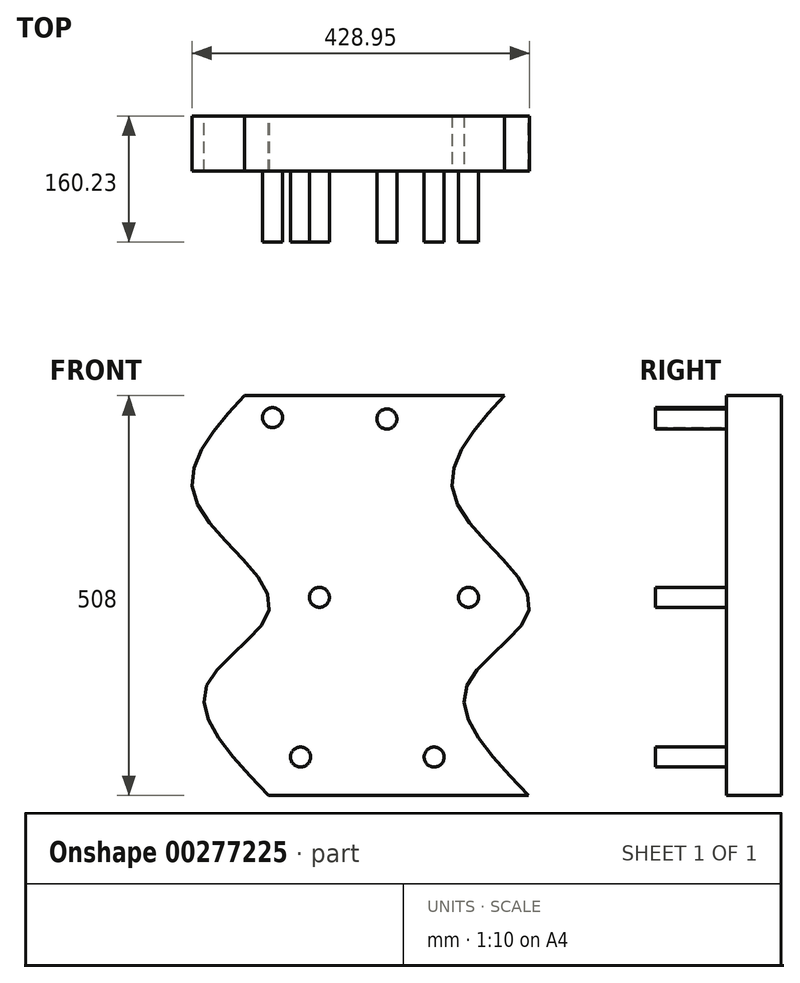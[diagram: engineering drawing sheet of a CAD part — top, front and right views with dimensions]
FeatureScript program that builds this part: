
annotation { "Feature Type Name" : "Feature", "Feature Type Description" : "" }
export const myFeature = defineFeature(function(context is Context, id is Id, definition is map)
    precondition{}
    {
        {
            var Q0;
            Q0=qCreatedBy(makeId("Front.planeOp"),FACE);
            var sketch = newSketch(context, id + "F0", { "sketchPlane" : qUnion([Q0])});
            skFitSpline(sketch, "E0", {"points": [v(-78.93, 247.75) * mm, v(-142.45, 117.9) * mm, v(-47.17, -18.48) * mm, v(-127.5, -122.17) * mm, v(-48.38, -260.25) * mm], "startDerivative": vector(-483.06, -524.92) * mm, "endDerivative": vector(549.76, -567.1) * mm});
            skFitSpline(sketch, "E1", {"points": [v(251.27, 247.75) * mm, v(187.75, 117.9) * mm, v(283.03, -18.48) * mm, v(202.7, -122.17) * mm, v(281.82, -260.25) * mm], "startDerivative": vector(-483.06, -524.92) * mm, "endDerivative": vector(549.76, -567.1) * mm});
            skLineSegment(sketch, "E2", {"start": v(-78.93, 247.75) * mm, "end": v(251.27, 247.75) * mm});
            skLineSegment(sketch, "E3", {"start": v(281.82, -260.25) * mm, "end": v(-48.38, -260.25) * mm});
            skSolve(sketch);
        }
        {
            var Q0;
            Q0 = qSketchRegion(id + "F0", true);
            extrude(context, id + "F1", {"entities" : qUnion([Q0]), "depth" : 70.23 * mm});
        }
        {
            var Q0;
            Q0=makeQuery(id+"F1.opExtrude","CAP_FACE",FACE,{"disambiguationData":[OSD([sQuery(id+"F0.wireOp",EDGE,"E0"),sQuery(id+"F0.wireOp",EDGE,"E1"),sQuery(id+"F0.wireOp",EDGE,"E2"),sQuery(id+"F0.wireOp",EDGE,"E3")])],"isStart":false});
            var sketch = newSketch(context, id + "F2", { "sketchPlane" : qUnion([Q0])});
            skCircle(sketch, "E4", {"center": v(-43.4, 219.81) * mm, "radius": 12.7 * mm});
            skCircle(sketch, "E5", {"center": v(101.79, 218.06) * mm, "radius": 12.7 * mm});
            skCircle(sketch, "E6", {"center": v(205.58, -8.6) * mm, "radius": 12.7 * mm});
            skCircle(sketch, "E7", {"center": v(161.82, -211.47) * mm, "radius": 12.7 * mm});
            skCircle(sketch, "E8", {"center": v(-7.78, -211.42) * mm, "radius": 12.7 * mm});
            skLineSegment(sketch, "E9", {"start": v(205.58, -8.6) * mm, "end": v(16.2, -8.6) * mm});
            skCircle(sketch, "E10", {"center": v(16.2, -8.6) * mm, "radius": 12.7 * mm});
            skSolve(sketch);
        }
        {
            var Q0;
            Q0=makeQuery(id+"F2.imprint","IMPRINT",FACE,{"disambiguationData":[TD([[makeQuery(id+"F2.imprint","IMPRINT",EDGE,{"derivedFrom":sQuery(id+"F2.wireOp",EDGE,"E4")}),1.0]])]});
            var Q1;
            Q1=makeQuery(id+"F2.imprint","IMPRINT",FACE,{"disambiguationData":[TD([[makeQuery(id+"F2.imprint","IMPRINT",EDGE,{"derivedFrom":sQuery(id+"F2.wireOp",EDGE,"E6")}),1.0]])]});
            var Q2;
            Q2=makeQuery(id+"F2.imprint","IMPRINT",FACE,{"disambiguationData":[TD([[makeQuery(id+"F2.imprint","IMPRINT",EDGE,{"derivedFrom":sQuery(id+"F2.wireOp",EDGE,"E10")}),1.0]])]});
            var Q3;
            Q3=makeQuery(id+"F2.imprint","IMPRINT",FACE,{"disambiguationData":[TD([[makeQuery(id+"F2.imprint","IMPRINT",EDGE,{"derivedFrom":sQuery(id+"F2.wireOp",EDGE,"E5")}),1.0]])]});
            var Q4;
            Q4=makeQuery(id+"F2.imprint","IMPRINT",FACE,{"disambiguationData":[TD([[makeQuery(id+"F2.imprint","IMPRINT",EDGE,{"derivedFrom":sQuery(id+"F2.wireOp",EDGE,"E7")}),1.0]])]});
            var Q5;
            Q5=makeQuery(id+"F2.imprint","IMPRINT",FACE,{"disambiguationData":[TD([[makeQuery(id+"F2.imprint","IMPRINT",EDGE,{"derivedFrom":sQuery(id+"F2.wireOp",EDGE,"E8")}),1.0]])]});
            extrude(context, id + "F3", {"entities" : qUnion([Q0, Q1, Q2, Q3, Q4, Q5]), "operationType" : NewBodyOperationType.ADD, "depth" : 90 * mm});
        }
    });
